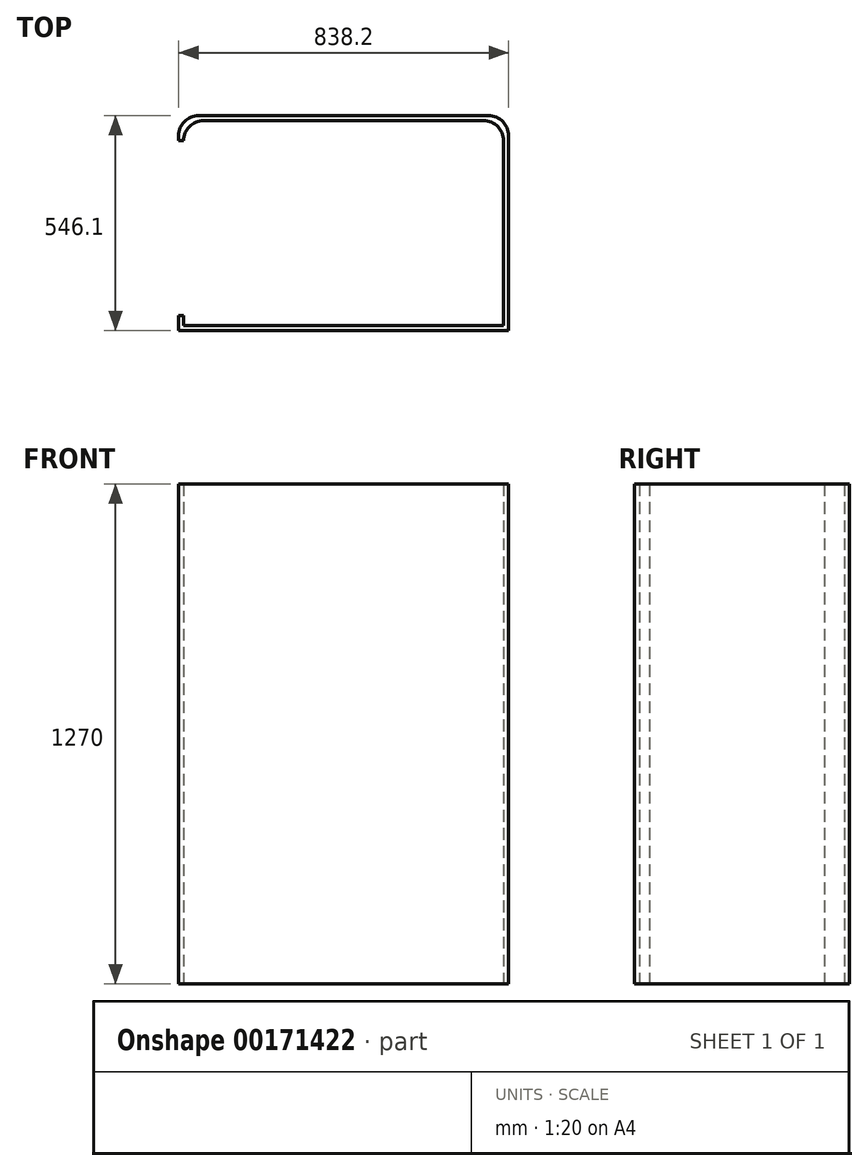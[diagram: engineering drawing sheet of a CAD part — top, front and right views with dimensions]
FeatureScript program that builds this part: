
annotation { "Feature Type Name" : "Feature", "Feature Type Description" : "" }
export const myFeature = defineFeature(function(context is Context, id is Id, definition is map)
    precondition{}
    {
        {
            var Q0;
            Q0=qCreatedBy(makeId("Top.planeOp"),FACE);
            var sketch = newSketch(context, id + "F0", { "sketchPlane" : qUnion([Q0])});
            skLineSegment(sketch, "E0.bottom", {"start": v(-419.1, 6.35) * mm, "end": v(419.1, 6.35) * mm});
            skLineSegment(sketch, "E0.top", {"start": v(-419.1, -6.35) * mm, "end": v(419.1, -6.35) * mm});
            skLineSegment(sketch, "E0.left", {"start": v(-419.1, 6.35) * mm, "end": v(-419.1, -6.35) * mm});
            skLineSegment(sketch, "E0.right", {"start": v(419.1, 6.35) * mm, "end": v(419.1, -6.35) * mm});
            skPoint(sketch, "E0.middle", {"position": v(0, 0) * mm});
            skLineSegment(sketch, "E1", {"start": v(419.1, 6.35) * mm, "end": v(419.1, 488.95) * mm});
            skLineSegment(sketch, "E2", {"start": v(368.3, 539.75) * mm, "end": v(-368.3, 539.75) * mm});
            skLineSegment(sketch, "E3", {"start": v(-419.1, 6.35) * mm, "end": v(-419.1, 31.75) * mm});
            skLineSegment(sketch, "E4", {"start": v(-419.1, 31.75) * mm, "end": v(-406.4, 31.75) * mm});
            skLineSegment(sketch, "E5", {"start": v(406.4, 6.35) * mm, "end": v(406.4, 476.25) * mm});
            skLineSegment(sketch, "E6", {"start": v(355.6, 527.05) * mm, "end": v(-355.6, 527.05) * mm});
            skLineSegment(sketch, "E7", {"start": v(-406.4, 31.75) * mm, "end": v(-406.4, 6.35) * mm});
            skPoint(sketch, "E8.visualSharp", {"position": v(419.1, 539.75) * mm});
            skArc(sketch, "E8.filletArc", {"start": v(419.1, 488.95) * mm, "mid": v(404.22, 524.87) * mm, "end": v(368.3, 539.75) * mm});
            skPoint(sketch, "E9.visualSharp", {"position": v(406.4, 527.05) * mm});
            skArc(sketch, "E9.filletArc", {"start": v(406.4, 476.25) * mm, "mid": v(391.52, 512.17) * mm, "end": v(355.6, 527.05) * mm});
            skPoint(sketch, "E10.visualSharp", {"position": v(0, 857.76) * mm});
            skPoint(sketch, "E11.visualSharp", {"position": v(-15.65, 848.95) * mm});
            skLineSegment(sketch, "E12", {"start": v(-419.1, 527.05) * mm, "end": v(-419.1, 476.25) * mm});
            skLineSegment(sketch, "E13", {"start": v(-406.4, 476.25) * mm, "end": v(-406.4, 476.25) * mm});
            skLineSegment(sketch, "E14", {"start": v(-419.1, 476.25) * mm, "end": v(-406.4, 476.25) * mm});
            skLineSegment(sketch, "E15", {"start": v(-419.1, 527.05) * mm, "end": v(-419.1, 488.95) * mm});
            skPoint(sketch, "E16.visualSharp", {"position": v(-419.1, 539.75) * mm});
            skArc(sketch, "E16.filletArc", {"start": v(-368.3, 539.75) * mm, "mid": v(-404.22, 524.87) * mm, "end": v(-419.1, 488.95) * mm});
            skPoint(sketch, "E17.newPointA", {"position": v(-419.1, 527.05) * mm});
            skPoint(sketch, "E17.newPointB", {"position": v(-406.4, 527.05) * mm});
            skArc(sketch, "E17.filletArc", {"start": v(-355.6, 527.05) * mm, "mid": v(-391.52, 512.17) * mm, "end": v(-406.4, 476.25) * mm});
            skSolve(sketch);
        }
        {
            var Q0;
            Q0=qSketchRegion(id+"F0",true);
            extrude(context, id + "F1", {"entities" : qUnion([Q0]), "depth" : 1270 * mm});
        }
    });
